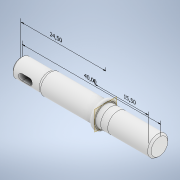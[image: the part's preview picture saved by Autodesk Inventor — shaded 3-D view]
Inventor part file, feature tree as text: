
AUTODESK INVENTOR PART (.ipt)
format: ipt  version: 2022.6 (Build 266554000, 554)  size: 219,648 bytes
history: native  units: mm
features: other x6, extrude x5, plane x2, fillet x2, projected_geometry x2, loft x1, chamfer x1
ambient origin geometry x8: Origin, YZ Plane, XZ Plane, XY Plane, X Axis, Y Axis, Z Axis, Center Point
bodies: Solid1 (feature_tree)
feature tree (19):
  other  "Annotations"
  extrude  "Shaft"  TaperAngle=0.0deg  [1 undecoded]
  extrude  "Slot for Differential Gear"  Depth=2.35mm TaperAngle=0.0deg
  plane  "Work Plane1"
  extrude  "Wheel Insert Profile"  Depth=1.8mm
  loft  "Loft1"
  plane  "Work Plane2"
  extrude  "Stopper"  Depth=1.0mm
  fillet  "Fillet1"  Radius=7.0mm
  extrude  "Differential Gear Insert Profile"  Depth=12.0mm TaperAngle=0.0deg
  fillet  "Fillet3"  Radius=2.0mm
  chamfer  "Chamfer4"  Distance=7.5mm
  projected_geometry  "Projected Loop1"
  other  "Edges2"
  other  "Edges4"
  projected_geometry  "Project Cut Edges1"
  other  "Linear Dimension 1"
  other  "Linear Dimension 2"
  other  "Linear Dimension 3"
note: 1 required parameter value undecoded (feature->parameter linkage not recoverable at this tier; creation-order binding heuristic only, values carry confidence <= 0.55)
